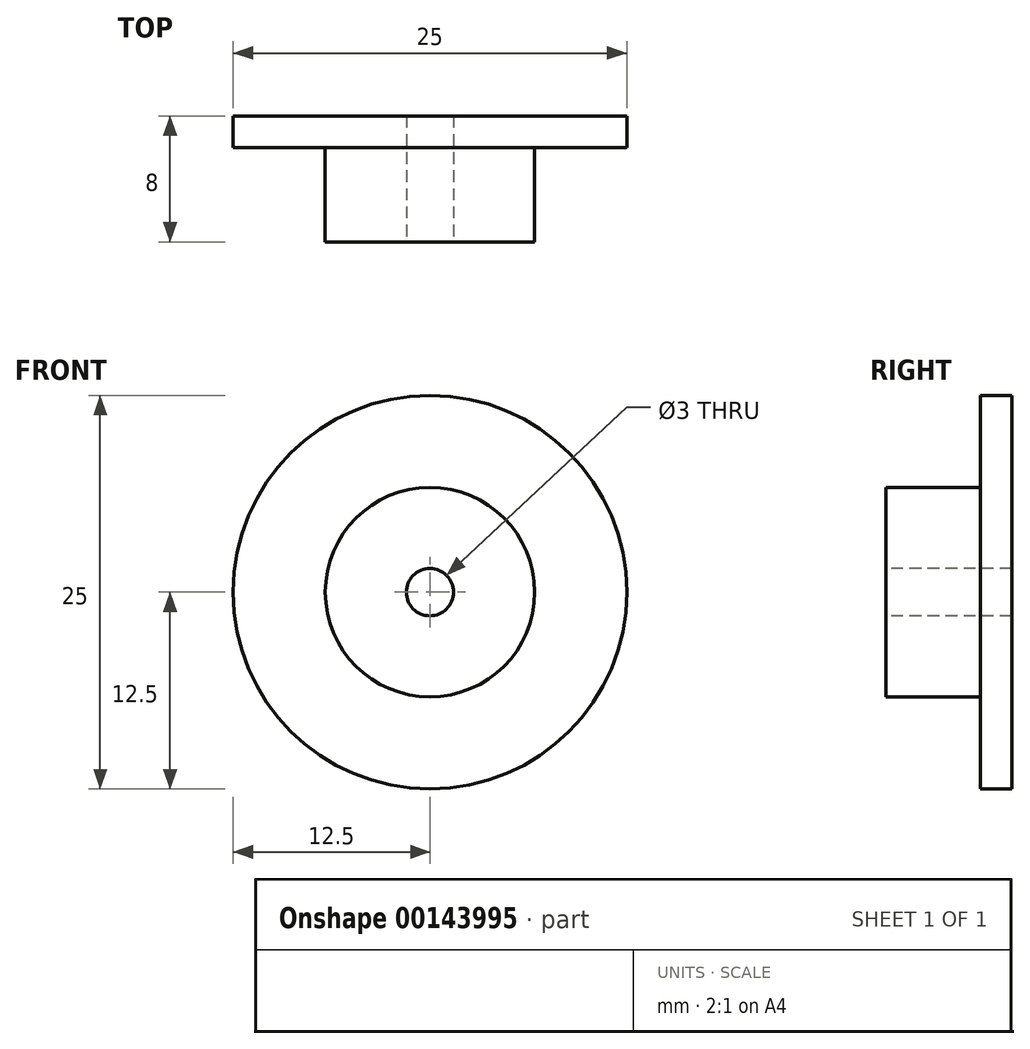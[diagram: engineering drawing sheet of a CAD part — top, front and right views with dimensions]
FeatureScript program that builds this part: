
annotation { "Feature Type Name" : "Feature", "Feature Type Description" : "" }
export const myFeature = defineFeature(function(context is Context, id is Id, definition is map)
    precondition{}
    {
        {
            var Q0;
            Q0=qCreatedBy(makeId("Front.planeOp"),FACE);
            var sketch = newSketch(context, id + "F0", { "sketchPlane" : qUnion([Q0])});
            skCircle(sketch, "E0", {"center": v(0, 0) * mm, "radius": 12.5 * mm});
            skSolve(sketch);
        }
        {
            var Q0;
            Q0=qSketchRegion(id+"F0",true);
            extrude(context, id + "F1", {"entities" : qUnion([Q0]), "depth" : 2 * mm});
        }
        {
            var Q0;
            Q0=makeQuery(id+"F1.opExtrude","CAP_FACE",FACE,{"disambiguationData":[OSD([sQuery(id+"F0.wireOp",EDGE,"E0")])],"isStart":false});
            var sketch = newSketch(context, id + "F2", { "sketchPlane" : qUnion([Q0])});
            skCircle(sketch, "E1", {"center": v(0, 0) * mm, "radius": 6.65 * mm});
            skSolve(sketch);
        }
        {
            var Q0;
            Q0=qSketchRegion(id+"F2",true);
            extrude(context, id + "F3", {"entities" : qUnion([Q0]), "operationType" : NewBodyOperationType.ADD, "depth" : 6 * mm});
        }
        {
            var Q0;
            Q0=makeQuery(id+"F3.opExtrude","CAP_FACE",FACE,{"disambiguationData":[OSD([sQuery(id+"F2.wireOp",EDGE,"E1")])],"isStart":false});
            var sketch = newSketch(context, id + "F4", { "sketchPlane" : qUnion([Q0])});
            skCircle(sketch, "E2", {"center": v(0, 0) * mm, "radius": 1.5 * mm});
            skSolve(sketch);
        }
        {
            var Q0;
            Q0=qSketchRegion(id+"F4",true);
            extrude(context, id + "F5", {"entities" : qUnion([Q0]), "operationType" : NewBodyOperationType.REMOVE, "endBound" : BoundingType.THROUGH_ALL, "oppositeDirection" : true, "depth" : 25 * mm});
        }
    });
